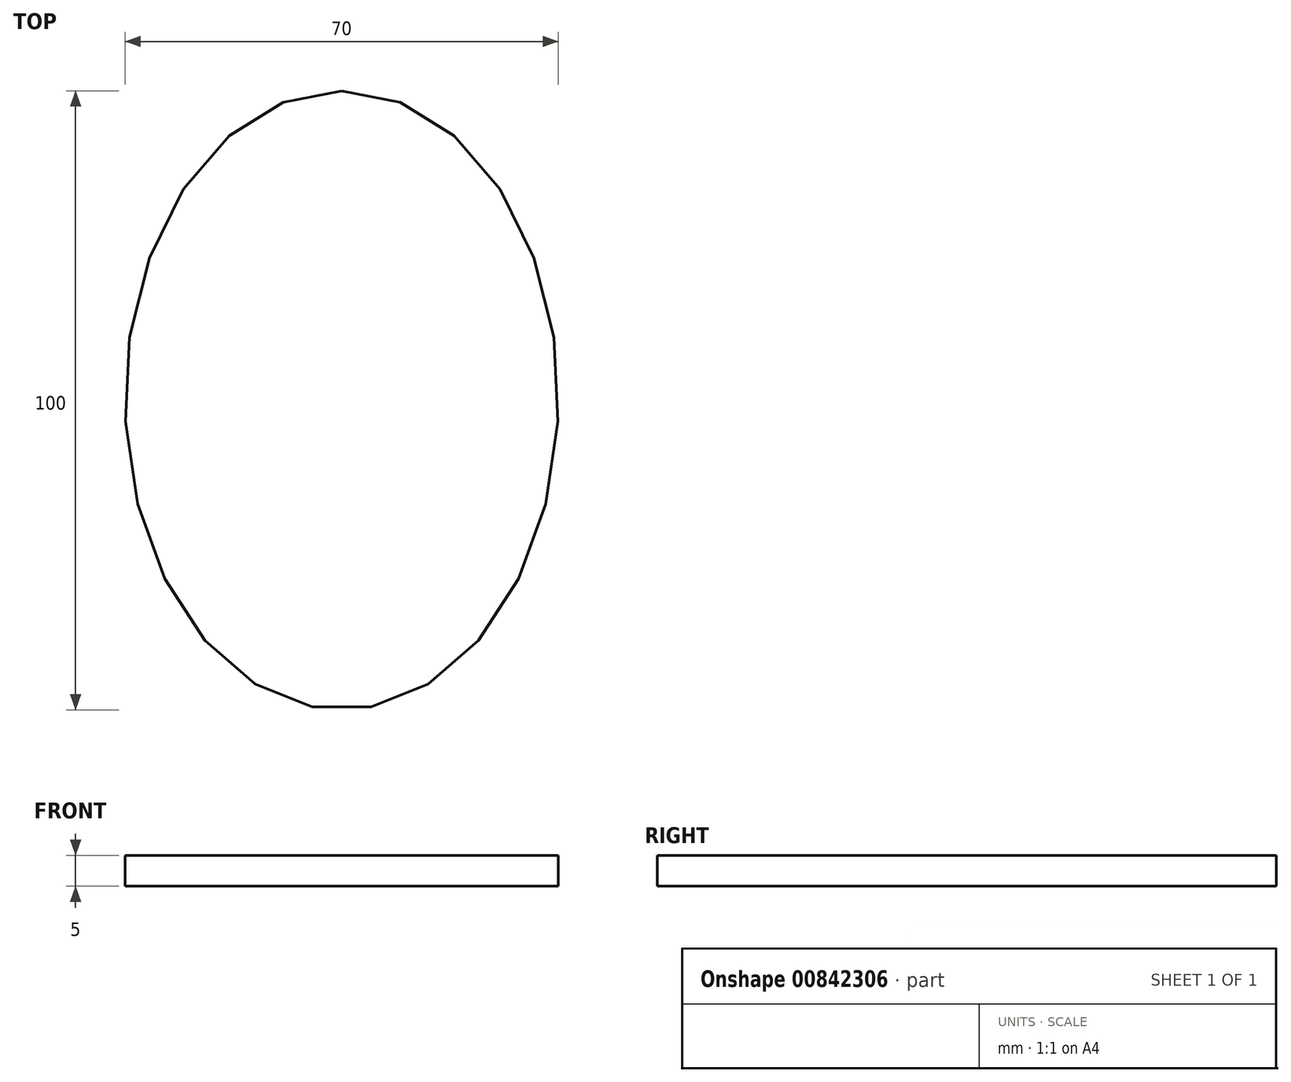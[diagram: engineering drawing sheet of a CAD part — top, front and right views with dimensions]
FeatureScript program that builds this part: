
annotation { "Feature Type Name" : "Feature", "Feature Type Description" : "" }
export const myFeature = defineFeature(function(context is Context, id is Id, definition is map)
    precondition{}
    {
        {
            var Q0;
            Q0=qCreatedBy(makeId("Top.planeOp"),FACE);
            var sketch = newSketch(context, id + "F0", { "sketchPlane" : qUnion([Q0])});
            skEllipse(sketch, "E0", {"center": v(0, 0) * mm, "majorRadius": 50 * mm, "minorRadius": 35 * mm, "majorAxis": v(0, 1)});
            skSolve(sketch);
        }
        {
            var Q0;
            Q0=makeQuery(id+"F0.imprint","IMPRINT",FACE,{"disambiguationData":[TD([[makeQuery(id+"F0.imprint","IMPRINT",EDGE,{"derivedFrom":sQuery(id+"F0.wireOp",EDGE,"E0")}),1.0]])]});
            extrude(context, id + "F1", {"entities" : qUnion([Q0]), "depth" : 5 * mm, "offsetDistance" : 25 * mm});
        }
    });
